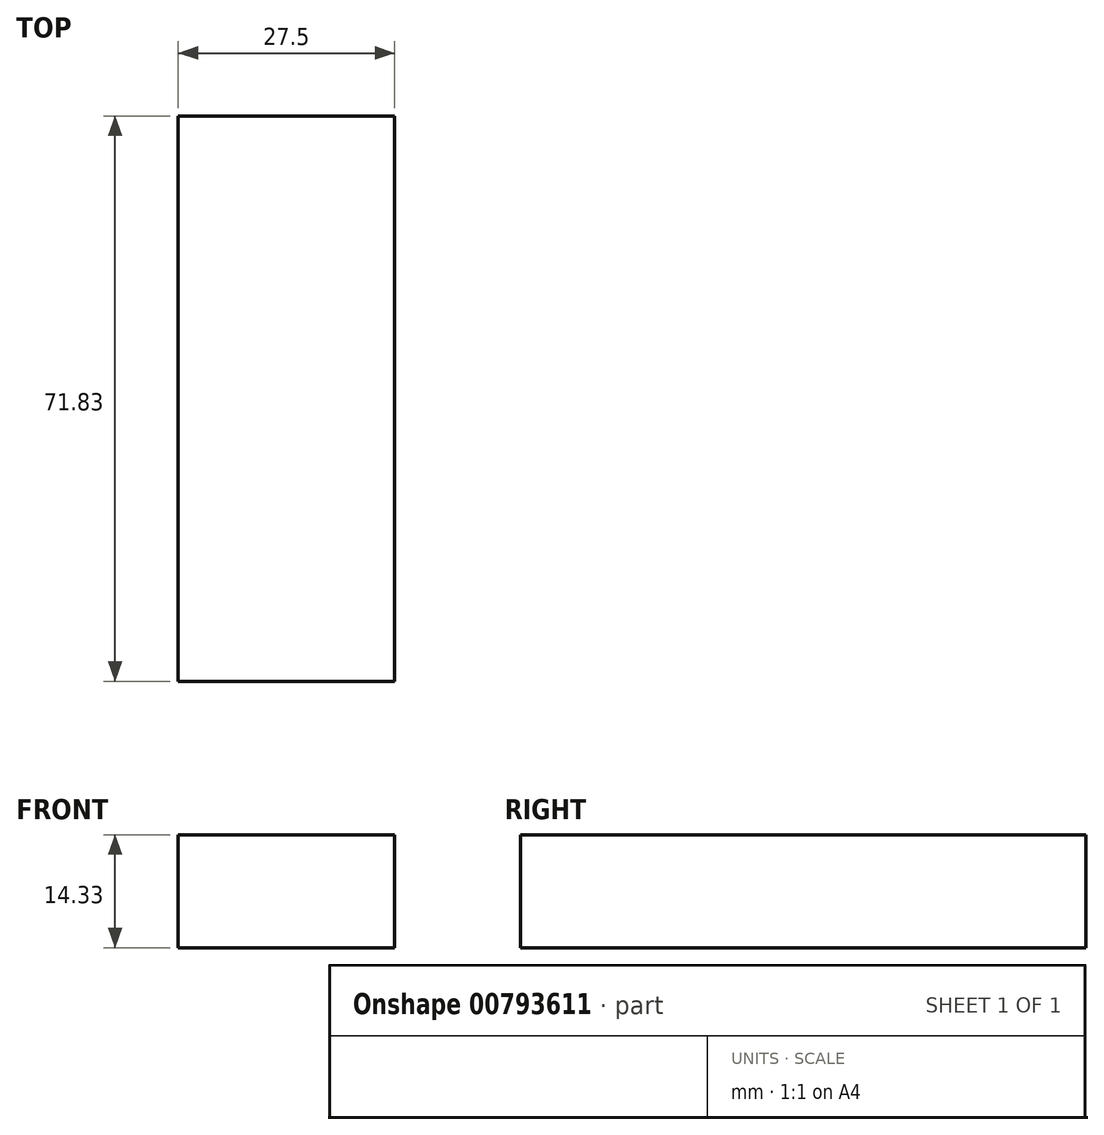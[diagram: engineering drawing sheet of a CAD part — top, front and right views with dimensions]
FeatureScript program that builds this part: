
annotation { "Feature Type Name" : "Feature", "Feature Type Description" : "" }
export const myFeature = defineFeature(function(context is Context, id is Id, definition is map)
    precondition{}
    {
        {
            var Q0;
            Q0=qCreatedBy(makeId("Front.planeOp"),FACE);
            var sketch = newSketch(context, id + "F0", { "sketchPlane" : qUnion([Q0])});
            skLineSegment(sketch, "E0.bottom", {"start": v(40.3, 0) * mm, "end": v(34.81, 0) * mm});
            skLineSegment(sketch, "E0.top", {"start": v(40.3, -47.67) * mm, "end": v(34.81, -47.67) * mm});
            skLineSegment(sketch, "E0.left", {"start": v(40.3, 0) * mm, "end": v(40.3, -47.67) * mm});
            skLineSegment(sketch, "E0.right", {"start": v(34.81, 0) * mm, "end": v(34.81, -47.67) * mm});
            skPoint(sketch, "E1.firstSnap0", {"position": v(34.81, -23.84) * mm});
            skPoint(sketch, "E1.oppositeSnap0", {"position": v(34.81, -23.84) * mm});
            skLineSegment(sketch, "E1.bottom", {"start": v(8.21, -23.84) * mm, "end": v(7.3, -23.84) * mm});
            skLineSegment(sketch, "E1.top", {"start": v(8.21, -23.84) * mm, "end": v(7.3, -23.84) * mm});
            skLineSegment(sketch, "E1.left", {"start": v(8.21, -23.84) * mm, "end": v(8.21, -23.84) * mm});
            skLineSegment(sketch, "E1.right", {"start": v(7.3, -23.84) * mm, "end": v(7.3, -23.84) * mm});
            skLineSegment(sketch, "E2.bottom", {"start": v(34.81, -38.17) * mm, "end": v(7.3, -38.17) * mm});
            skLineSegment(sketch, "E2.top", {"start": v(34.81, -23.84) * mm, "end": v(7.3, -23.84) * mm});
            skLineSegment(sketch, "E2.left", {"start": v(34.81, -38.17) * mm, "end": v(34.81, -23.84) * mm});
            skLineSegment(sketch, "E2.right", {"start": v(7.3, -38.17) * mm, "end": v(7.3, -23.84) * mm});
            skLineSegment(sketch, "E3.bottom", {"start": v(21.06, -23.84) * mm, "end": v(8.21, -23.84) * mm});
            skLineSegment(sketch, "E3.top", {"start": v(21.06, -23.84) * mm, "end": v(8.21, -23.84) * mm});
            skLineSegment(sketch, "E3.left", {"start": v(21.06, -23.84) * mm, "end": v(21.06, -23.84) * mm});
            skSolve(sketch);
        }
        {
            var Q0;
            Q0=makeQuery(id+"F0.imprint","IMPRINT",FACE,{"disambiguationData":[TD([[makeQuery(id+"F0.imprint","IMPRINT",EDGE,{"derivedFrom":sQuery(id+"F0.wireOp",EDGE,"E2.bottom")}),-1.0]])]});
            extrude(context, id + "F1", {"entities" : qUnion([Q0]), "depth" : 71.83 * mm, "offsetDistance" : 25.4 * mm});
        }
    });
